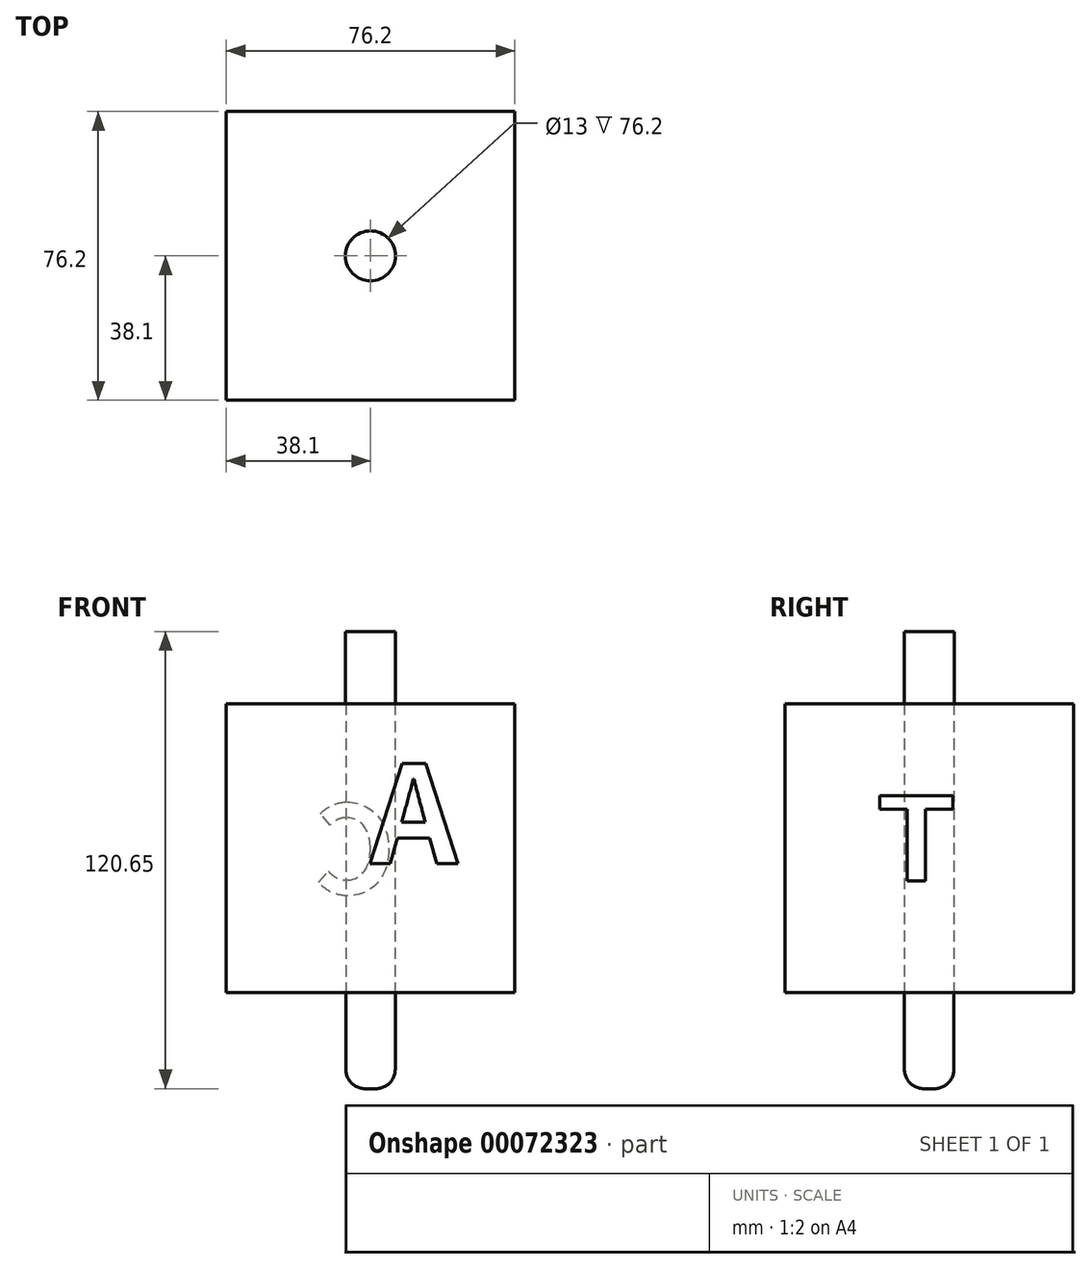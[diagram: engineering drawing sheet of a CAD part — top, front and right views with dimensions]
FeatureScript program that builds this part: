
annotation { "Feature Type Name" : "Feature", "Feature Type Description" : "" }
export const myFeature = defineFeature(function(context is Context, id is Id, definition is map)
    precondition{}
    {
        {
            var Q0;
            Q0=qCreatedBy(makeId("Top.planeOp"),FACE);
            var sketch = newSketch(context, id + "F0", { "sketchPlane" : qUnion([Q0])});
            skLineSegment(sketch, "E0.rect.bottom", {"start": v(38.1, -38.1) * mm, "end": v(-38.1, -38.1) * mm});
            skLineSegment(sketch, "E0.rect.top", {"start": v(38.1, 38.1) * mm, "end": v(-38.1, 38.1) * mm});
            skLineSegment(sketch, "E0.rect.left", {"start": v(38.1, -38.1) * mm, "end": v(38.1, 38.1) * mm});
            skLineSegment(sketch, "E0.rect.right", {"start": v(-38.1, -38.1) * mm, "end": v(-38.1, 38.1) * mm});
            skPoint(sketch, "E0.rect.middle", {"position": v(0, 0) * mm});
            skCircle(sketch, "E1", {"center": v(0, 0) * mm, "radius": 6.5 * mm});
            skSolve(sketch);
        }
        {
            var Q0;
            Q0=makeQuery(id+"F0.imprint","IMPRINT",FACE,{"disambiguationData":[TD([[makeQuery(id+"F0.imprint","IMPRINT",EDGE,{"derivedFrom":sQuery(id+"F0.wireOp",EDGE,"E0.rect.bottom")}),-1.0]])]});
            extrude(context, id + "F1", {"entities" : qUnion([Q0]), "depth" : 76.2 * mm});
        }
        {
            var Q0;
            Q0=makeQuery(id+"F1.opExtrude","SWEPT_FACE",FACE,{"disambiguationData":[OSD([sQuery(id+"F0.wireOp",EDGE,"E0.rect.bottom")])]});
            var sketch = newSketch(context, id + "F2", { "sketchPlane" : qUnion([Q0])});
            skText(sketch, "E2", { "text": "A", "fontName": "NotoSansCJKkr-Bold.otf"});
            const initialGuessF2  = {"E2": [0, 0.03396, 1, 0, 0.02573]};
            skSetInitialGuess(sketch, initialGuessF2);
            skSolve(sketch);
        }
        {
            var Q0;
            Q0=makeQuery(id+"F2.imprint","IMPRINT",FACE,{"disambiguationData":[TD([[makeQuery(id+"F2.imprint","IMPRINT",EDGE,{"derivedFrom":sQuery(id+"F2.wireOp",EDGE,"E2.sketch_text.stroke-0")}),1.0]])]});
            extrude(context, id + "F3", {"entities" : qUnion([Q0]), "operationType" : NewBodyOperationType.REMOVE, "oppositeDirection" : true, "depth" : 1 / 101.6 * mm});
        }
        {
            var Q0;
            Q0=makeQuery(id+"F1.opExtrude","SWEPT_FACE",FACE,{"disambiguationData":[OSD([sQuery(id+"F0.wireOp",EDGE,"E0.rect.left")])]});
            var sketch = newSketch(context, id + "F4", { "sketchPlane" : qUnion([Q0])});
            skText(sketch, "E3", { "text": "T", "fontName": "NotoSans-Bold.ttf"});
            const initialGuessF4  = {"E3": [-0.01207, 0.0344, 1, 0, 0.02382]};
            skSetInitialGuess(sketch, initialGuessF4);
            skSolve(sketch);
        }
        {
            var Q0;
            Q0=makeQuery(id+"F4.imprint","IMPRINT",FACE,{"disambiguationData":[TD([[makeQuery(id+"F4.imprint","IMPRINT",EDGE,{"derivedFrom":sQuery(id+"F4.wireOp",EDGE,"E3.sketch_text.stroke-0")}),-1.0]])]});
            extrude(context, id + "F5", {"entities" : qUnion([Q0]), "operationType" : NewBodyOperationType.REMOVE, "depth" : 1 / 101.6 * mm});
        }
        {
            var Q0;
            Q0=makeQuery(id+"F1.opExtrude","SWEPT_FACE",FACE,{"disambiguationData":[OSD([sQuery(id+"F0.wireOp",EDGE,"E0.rect.left")])]});
            var sketch = newSketch(context, id + "F6", { "sketchPlane" : qUnion([Q0])});
            skText(sketch, "E4", { "text": "T", "fontName": "Arimo-Bold.ttf"});
            const initialGuessF6  = {"E4": [-0.01338, 0.02944, 1, 0, 0.02354]};
            skSetInitialGuess(sketch, initialGuessF6);
            skSolve(sketch);
        }
        {
            var Q0;
            Q0=makeQuery(id+"F6.imprint","IMPRINT",FACE,{"disambiguationData":[TD([[makeQuery(id+"F6.imprint","IMPRINT",EDGE,{"derivedFrom":sQuery(id+"F6.wireOp",EDGE,"E4.sketch_text.stroke-0")}),-1.0]])]});
            extrude(context, id + "F7", {"entities" : qUnion([Q0]), "operationType" : NewBodyOperationType.REMOVE, "oppositeDirection" : true, "depth" : 1 / 101.6 * mm});
        }
        {
            var Q0;
            Q0=makeQuery(id+"F1.opExtrude","SWEPT_FACE",FACE,{"disambiguationData":[OSD([sQuery(id+"F0.wireOp",EDGE,"E0.rect.top")])]});
            var sketch = newSketch(context, id + "F8", { "sketchPlane" : qUnion([Q0])});
            skText(sketch, "E5", { "text": "C", "fontName": "NotoSansCJKsc-Bold.otf"});
            const initialGuessF8  = {"E5": [-0.00656, 0.02596, 1, 0, 0.02316]};
            skSetInitialGuess(sketch, initialGuessF8);
            skSolve(sketch);
        }
        {
            var Q0;
            Q0=makeQuery(id+"F8.imprint","IMPRINT",FACE,{"disambiguationData":[TD([[makeQuery(id+"F8.imprint","IMPRINT",EDGE,{"derivedFrom":sQuery(id+"F8.wireOp",EDGE,"E5.sketch_text.stroke-0")}),1.0]])]});
            extrude(context, id + "F9", {"entities" : qUnion([Q0]), "operationType" : NewBodyOperationType.REMOVE, "oppositeDirection" : true, "depth" : 1 / 101.6 * mm});
        }
        {
            var Q0;
            Q0=makeQuery(id+"F1.opExtrude","CAP_FACE",FACE,{"disambiguationData":[OSD([sQuery(id+"F0.wireOp",EDGE,"E0.rect.bottom"),sQuery(id+"F0.wireOp",EDGE,"E0.rect.top"),sQuery(id+"F0.wireOp",EDGE,"E0.rect.left"),sQuery(id+"F0.wireOp",EDGE,"E0.rect.right"),sQuery(id+"F0.wireOp",EDGE,"E1")])],"isStart":false});
            var sketch = newSketch(context, id + "F10", { "sketchPlane" : qUnion([Q0])});
            skCircle(sketch, "E6", {"center": v(0, 0) * mm, "radius": 6.6 * mm});
            skSolve(sketch);
        }
        {
            var Q0;
            Q0 = qSketchRegion(id + "F10", true);
            extrude(context, id + "F11", {"entities" : qUnion([Q0]), "operationType" : NewBodyOperationType.ADD, "depth" : 19.05 * mm});
        }
        {
            var Q0;
            Q0=makeQuery(id+"F1.opExtrude","CAP_FACE",FACE,{"disambiguationData":[OSD([sQuery(id+"F0.wireOp",EDGE,"E0.rect.bottom"),sQuery(id+"F0.wireOp",EDGE,"E0.rect.top"),sQuery(id+"F0.wireOp",EDGE,"E0.rect.left"),sQuery(id+"F0.wireOp",EDGE,"E0.rect.right"),sQuery(id+"F0.wireOp",EDGE,"E1")])],"isStart":true});
            var sketch = newSketch(context, id + "F12", { "sketchPlane" : qUnion([Q0])});
            skCircle(sketch, "E7", {"center": v(0, 0) * mm, "radius": 6.52 * mm});
            skSolve(sketch);
        }
        {
            var Q0;
            Q0 = qSketchRegion(id + "F12", true);
            extrude(context, id + "F13", {"entities" : qUnion([Q0]), "operationType" : NewBodyOperationType.ADD, "depth" : 25.4 * mm});
        }
        {
            var Q0;
            Q0=makeQuery(id+"F13.opExtrude","CAP_EDGE",EDGE,{"disambiguationData":[OSD([sQuery(id+"F12.wireOp",EDGE,"E7")])],"isStart":false});
            fillet(context, id + "F14", {"entities" : qUnion([Q0]), "radius" : 5.08 * mm, "tangentPropagation" : true, "allowEdgeOverflow" : false});
        }
    });
